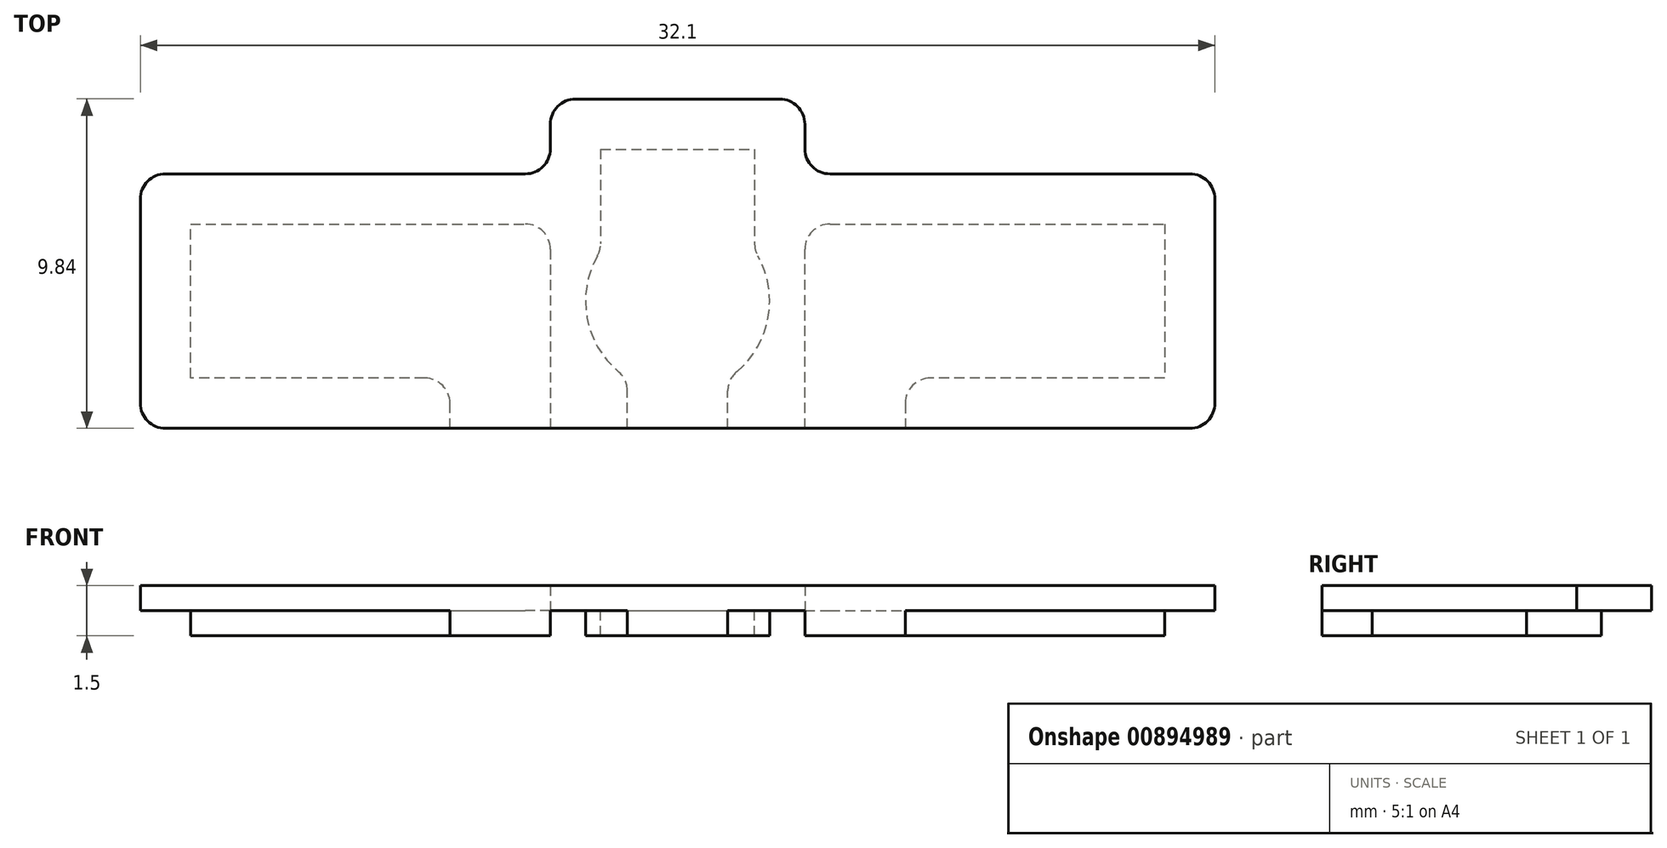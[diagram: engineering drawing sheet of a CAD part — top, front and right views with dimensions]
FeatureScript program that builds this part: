
annotation { "Feature Type Name" : "Feature", "Feature Type Description" : "" }
export const myFeature = defineFeature(function(context is Context, id is Id, definition is map)
    precondition{}
    {
        {
            var Q0;
            Q0=qCreatedBy(makeId("Top.planeOp"),FACE);
            var sketch = newSketch(context, id + "F0", { "sketchPlane" : qUnion([Q0])});
            skLineSegment(sketch, "E0.bottom", {"start": v(-15.1, 3.01) * mm, "end": v(-4.35, 3.01) * mm});
            skLineSegment(sketch, "E0.top", {"start": v(-15.1, -4.59) * mm, "end": v(15.5, -4.59) * mm});
            skLineSegment(sketch, "E0.left", {"start": v(-15.85, 2.26) * mm, "end": v(-15.85, -3.84) * mm});
            skLineSegment(sketch, "E0.right", {"start": v(16.25, 2.26) * mm, "end": v(16.25, -3.84) * mm});
            skPoint(sketch, "E0.middle", {"position": v(0.2, -0.79) * mm});
            skLineSegment(sketch, "E1.top", {"start": v(-2.85, 5.25) * mm, "end": v(3.25, 5.25) * mm});
            skLineSegment(sketch, "E1.left", {"start": v(-3.6, 3.76) * mm, "end": v(-3.6, 4.5) * mm});
            skLineSegment(sketch, "E1.right", {"start": v(4, 3.76) * mm, "end": v(4, 4.5) * mm});
            skLineSegment(sketch, "E2", {"start": v(-2.1, 3.75) * mm, "end": v(2.5, 3.75) * mm});
            skLineSegment(sketch, "E3", {"start": v(2.5, 3.75) * mm, "end": v(2.5, 0.93) * mm});
            skLineSegment(sketch, "E4", {"start": v(-2.1, 3.75) * mm, "end": v(-2.1, 0.93) * mm});
            skLineSegment(sketch, "E5", {"start": v(-1.3, -4.59) * mm, "end": v(-1.3, -3.47) * mm});
            skLineSegment(sketch, "E6", {"start": v(1.7, -4.59) * mm, "end": v(1.7, -3.47) * mm});
            skLineSegment(sketch, "E7", {"start": v(-14.35, -3.09) * mm, "end": v(-14.35, 1.51) * mm});
            skLineSegment(sketch, "E8", {"start": v(-14.35, 1.51) * mm, "end": v(-4.35, 1.51) * mm});
            skLineSegment(sketch, "E9", {"start": v(-3.6, 0.76) * mm, "end": v(-3.6, -4.59) * mm});
            skLineSegment(sketch, "E10", {"start": v(-7.35, -3.09) * mm, "end": v(-14.35, -3.09) * mm});
            skArc(sketch, "E11", {"start": v(-2.2, 0.56) * mm, "mid": v(-2.5, -1.28) * mm, "end": v(-1.57, -2.9) * mm});
            skLineSegment(sketch, "E12", {"start": v(4, -4.59) * mm, "end": v(4, 0.76) * mm});
            skLineSegment(sketch, "E13", {"start": v(4.75, 1.51) * mm, "end": v(14.75, 1.51) * mm});
            skLineSegment(sketch, "E14", {"start": v(14.75, 1.51) * mm, "end": v(14.75, -3.09) * mm});
            skLineSegment(sketch, "E15", {"start": v(14.75, -3.09) * mm, "end": v(7.75, -3.09) * mm});
            skLineSegment(sketch, "E16", {"start": v(7, -3.84) * mm, "end": v(7, -4.59) * mm});
            skLineSegment(sketch, "E17.trimOffspring", {"start": v(4.75, 3.01) * mm, "end": v(15.5, 3.01) * mm});
            skPoint(sketch, "E18.visualSharp", {"position": v(-3.6, 3.01) * mm});
            skArc(sketch, "E18.filletArc", {"start": v(-4.35, 3.01) * mm, "mid": v(-3.82, 3.23) * mm, "end": v(-3.6, 3.76) * mm});
            skPoint(sketch, "E19.visualSharp", {"position": v(-3.6, 5.25) * mm});
            skArc(sketch, "E19.filletArc", {"start": v(-2.85, 5.25) * mm, "mid": v(-3.38, 5.03) * mm, "end": v(-3.6, 4.5) * mm});
            skPoint(sketch, "E20.visualSharp", {"position": v(4, 5.25) * mm});
            skArc(sketch, "E20.filletArc", {"start": v(4, 4.5) * mm, "mid": v(3.78, 5.03) * mm, "end": v(3.25, 5.25) * mm});
            skPoint(sketch, "E21.visualSharp", {"position": v(4, 3.01) * mm});
            skArc(sketch, "E21.filletArc", {"start": v(4, 3.76) * mm, "mid": v(4.22, 3.23) * mm, "end": v(4.75, 3.01) * mm});
            skPoint(sketch, "E22.visualSharp", {"position": v(-3.6, 1.51) * mm});
            skArc(sketch, "E22.filletArc", {"start": v(-3.6, 0.76) * mm, "mid": v(-3.82, 1.3) * mm, "end": v(-4.35, 1.51) * mm});
            skPoint(sketch, "E23.newPointB", {"position": v(-15.85, 3.01) * mm});
            skPoint(sketch, "E24.visualSharp", {"position": v(-15.85, -4.59) * mm});
            skArc(sketch, "E24.filletArc", {"start": v(-15.85, -3.84) * mm, "mid": v(-15.63, -4.37) * mm, "end": v(-15.1, -4.59) * mm});
            skPoint(sketch, "E25.orphan", {"position": v(1.7, -0.79) * mm});
            skPoint(sketch, "E26.orphan", {"position": v(-1.3, -0.79) * mm});
            skPoint(sketch, "E27.trimOffspring.end.orphan", {"position": v(2.5, -4.59) * mm});
            skArc(sketch, "E28.trimOffspring", {"start": v(1.96, -2.9) * mm, "mid": v(2.9, -1.28) * mm, "end": v(2.6, 0.56) * mm});
            skPoint(sketch, "E29.visualSharp", {"position": v(4, 1.51) * mm});
            skArc(sketch, "E29.filletArc", {"start": v(4.75, 1.51) * mm, "mid": v(4.22, 1.3) * mm, "end": v(4, 0.76) * mm});
            skPoint(sketch, "E30.visualSharp", {"position": v(-2.1, 0.72) * mm});
            skArc(sketch, "E30.filletArc", {"start": v(-2.2, 0.56) * mm, "mid": v(-2.13, 0.74) * mm, "end": v(-2.1, 0.93) * mm});
            skPoint(sketch, "E31.visualSharp", {"position": v(2.5, 0.72) * mm});
            skArc(sketch, "E31.filletArc", {"start": v(2.5, 0.93) * mm, "mid": v(2.52, 0.74) * mm, "end": v(2.6, 0.56) * mm});
            skPoint(sketch, "E32.visualSharp", {"position": v(1.7, -3.1) * mm});
            skArc(sketch, "E32.filletArc", {"start": v(1.96, -2.9) * mm, "mid": v(1.77, -3.15) * mm, "end": v(1.7, -3.47) * mm});
            skPoint(sketch, "E33.visualSharp", {"position": v(-1.3, -3.1) * mm});
            skArc(sketch, "E33.filletArc", {"start": v(-1.3, -3.47) * mm, "mid": v(-1.37, -3.15) * mm, "end": v(-1.57, -2.9) * mm});
            skPoint(sketch, "E34.visualSharp", {"position": v(7, -3.09) * mm});
            skArc(sketch, "E34.filletArc", {"start": v(7.75, -3.09) * mm, "mid": v(7.22, -3.3) * mm, "end": v(7, -3.84) * mm});
            skPoint(sketch, "E35.visualSharp", {"position": v(16.25, 3.01) * mm});
            skArc(sketch, "E35.filletArc", {"start": v(16.25, 2.26) * mm, "mid": v(16.03, 2.8) * mm, "end": v(15.5, 3.01) * mm});
            skPoint(sketch, "E36.visualSharp", {"position": v(16.25, -4.59) * mm});
            skArc(sketch, "E36.filletArc", {"start": v(15.5, -4.59) * mm, "mid": v(16.03, -4.37) * mm, "end": v(16.25, -3.84) * mm});
            skArc(sketch, "E37.filletArc", {"start": v(-15.1, 3.01) * mm, "mid": v(-15.63, 2.8) * mm, "end": v(-15.85, 2.26) * mm});
            skLineSegment(sketch, "E38", {"start": v(-6.6, -4.59) * mm, "end": v(-6.6, -3.84) * mm});
            skPoint(sketch, "E39.visualSharp", {"position": v(-6.6, -3.09) * mm});
            skArc(sketch, "E39.filletArc", {"start": v(-6.6, -3.84) * mm, "mid": v(-6.82, -3.3) * mm, "end": v(-7.35, -3.09) * mm});
            skSolve(sketch);
        }
        {
            var Q0;
            Q0=makeQuery(id+"F0.imprint","IMPRINT",FACE,{"disambiguationData":[TD([[makeQuery(id+"F0.imprint","IMPRINT",EDGE,{"derivedFrom":sQuery(id+"F0.wireOp",EDGE,"E0.bottom")}),-1.0]])]});
            var Q1;
            Q1=makeQuery(id+"F0.imprint","IMPRINT",FACE,{"disambiguationData":[TD([[makeQuery(id+"F0.imprint","IMPRINT",EDGE,{"derivedFrom":sQuery(id+"F0.wireOp",EDGE,"E7")}),-1.0]])]});
            var Q2;
            {var subQ0=sQuery(id+"F0.wireOp",EDGE,"E12");Q2=makeQuery(id+"F0.imprint","IMPRINT",FACE,{"disambiguationData":[TD([[makeQuery(id+"F0.imprint","IMPRINT",EDGE,{"derivedFrom":subQ0}),-1.0]])]});}
            var Q3;
            Q3=makeQuery(id+"F0.imprint","IMPRINT",FACE,{"disambiguationData":[TD([[makeQuery(id+"F0.imprint","IMPRINT",EDGE,{"derivedFrom":sQuery(id+"F0.wireOp",EDGE,"E2")}),-1.0]])]});
            extrude(context, id + "F1", {"entities" : qUnion([Q0, Q1, Q2, Q3]), "depth" : .75 * mm, "offsetDistance" : 25 * mm});
        }
        {
            var Q0;
            Q0=makeQuery(id+"F0.imprint","IMPRINT",FACE,{"disambiguationData":[TD([[makeQuery(id+"F0.imprint","IMPRINT",EDGE,{"derivedFrom":sQuery(id+"F0.wireOp",EDGE,"E7")}),-1.0]])]});
            var Q1;
            Q1=makeQuery(id+"F0.imprint","IMPRINT",FACE,{"disambiguationData":[TD([[makeQuery(id+"F0.imprint","IMPRINT",EDGE,{"derivedFrom":sQuery(id+"F0.wireOp",EDGE,"E2")}),-1.0]])]});
            var Q2;
            {var subQ0=sQuery(id+"F0.wireOp",EDGE,"E12");Q2=makeQuery(id+"F0.imprint","IMPRINT",FACE,{"disambiguationData":[TD([[makeQuery(id+"F0.imprint","IMPRINT",EDGE,{"derivedFrom":subQ0}),-1.0]])]});}
            extrude(context, id + "F2", {"entities" : qUnion([Q0, Q1, Q2]), "operationType" : NewBodyOperationType.ADD, "oppositeDirection" : true, "depth" : .75 * mm, "offsetDistance" : 25 * mm});
        }
    });
